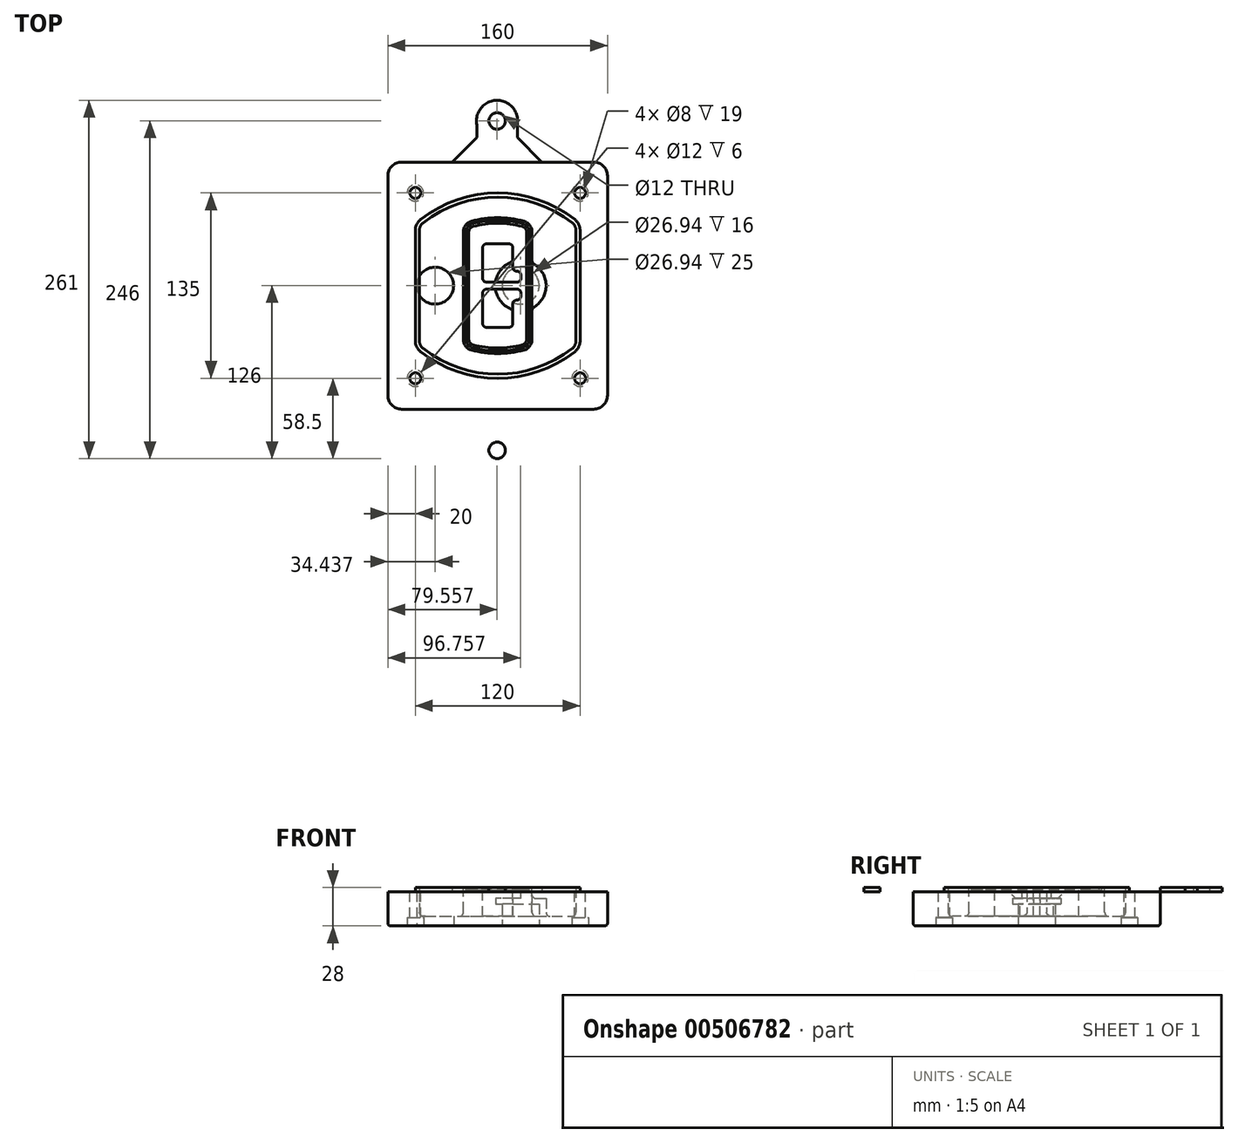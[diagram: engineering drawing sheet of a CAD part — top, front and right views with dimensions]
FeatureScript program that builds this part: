
annotation { "Feature Type Name" : "Feature", "Feature Type Description" : "" }
export const myFeature = defineFeature(function(context is Context, id is Id, definition is map)
    precondition{}
    {
        {
            var Q0;
            Q0=qCreatedBy(makeId("Top.planeOp"),FACE);
            var sketch = newSketch(context, id + "F0", { "sketchPlane" : qUnion([Q0])});
            skPoint(sketch, "E0.rect.middle", {"position": v(0, 0) * mm});
            skLineSegment(sketch, "E1.bottom", {"start": v(-70, -90) * mm, "end": v(70, -90) * mm});
            skLineSegment(sketch, "E1.top", {"start": v(-70, 90) * mm, "end": v(70, 90) * mm});
            skLineSegment(sketch, "E1.left", {"start": v(-80, -80) * mm, "end": v(-80, 80) * mm});
            skLineSegment(sketch, "E1.right", {"start": v(80, -80) * mm, "end": v(80, 80) * mm});
            skLineSegment(sketch, "E2", {"start": v(-80, 90) * mm, "end": v(80, -90) * mm, "construction": true});
            skLineSegment(sketch, "E3", {"start": v(80, 90) * mm, "end": v(-80, -90) * mm, "construction": true});
            skCircle(sketch, "E4", {"center": v(-60, 67.5) * mm, "radius": 4 * mm});
            skCircle(sketch, "E5", {"center": v(60, 67.5) * mm, "radius": 4 * mm});
            skCircle(sketch, "E6", {"center": v(60, -67.5) * mm, "radius": 4 * mm});
            skCircle(sketch, "E7", {"center": v(-60, -67.5) * mm, "radius": 4 * mm});
            skLineSegment(sketch, "E8", {"start": v(-60, 67.5) * mm, "end": v(60, 67.5) * mm, "construction": true});
            skLineSegment(sketch, "E9", {"start": v(60, 67.5) * mm, "end": v(60, -67.5) * mm, "construction": true});
            skLineSegment(sketch, "E10", {"start": v(60, -67.5) * mm, "end": v(-60, -67.5) * mm, "construction": true});
            skLineSegment(sketch, "E11", {"start": v(-60, -67.5) * mm, "end": v(-60, 67.5) * mm, "construction": true});
            skLineSegment(sketch, "E12", {"start": v(-60, 40.3) * mm, "end": v(-60, -40.3) * mm});
            skLineSegment(sketch, "E13", {"start": v(60, 40.3) * mm, "end": v(60, -40.3) * mm});
            skArc(sketch, "E14", {"start": v(56.15, 48.18) * mm, "mid": v(0, 67.5) * mm, "end": v(-56.15, 48.18) * mm});
            skArc(sketch, "E15", {"start": v(-56.15, -48.18) * mm, "mid": v(0, -67.5) * mm, "end": v(56.15, -48.18) * mm});
            skLineSegment(sketch, "E16", {"start": v(-60, 0) * mm, "end": v(60, 0) * mm, "construction": true});
            skPoint(sketch, "E17.visualSharp", {"position": v(-60, -45) * mm});
            skArc(sketch, "E17.filletArc", {"start": v(-60, -40.3) * mm, "mid": v(-58.99, -44.68) * mm, "end": v(-56.15, -48.18) * mm});
            skPoint(sketch, "E18.visualSharp", {"position": v(-60, 45) * mm});
            skArc(sketch, "E18.filletArc", {"start": v(-56.15, 48.18) * mm, "mid": v(-58.99, 44.68) * mm, "end": v(-60, 40.3) * mm});
            skPoint(sketch, "E19.visualSharp", {"position": v(60, 45) * mm});
            skArc(sketch, "E19.filletArc", {"start": v(60, 40.3) * mm, "mid": v(58.99, 44.68) * mm, "end": v(56.15, 48.18) * mm});
            skPoint(sketch, "E20.visualSharp", {"position": v(60, -45) * mm});
            skArc(sketch, "E20.filletArc", {"start": v(56.15, -48.18) * mm, "mid": v(58.99, -44.68) * mm, "end": v(60, -40.3) * mm});
            skPoint(sketch, "E21.visualSharp", {"position": v(-80, 90) * mm});
            skArc(sketch, "E21.filletArc", {"start": v(-70, 90) * mm, "mid": v(-77.07, 87.07) * mm, "end": v(-80, 80) * mm});
            skPoint(sketch, "E22.visualSharp", {"position": v(80, 90) * mm});
            skArc(sketch, "E22.filletArc", {"start": v(80, 80) * mm, "mid": v(77.07, 87.07) * mm, "end": v(70, 90) * mm});
            skPoint(sketch, "E23.visualSharp", {"position": v(80, -90) * mm});
            skArc(sketch, "E23.filletArc", {"start": v(70, -90) * mm, "mid": v(77.07, -87.07) * mm, "end": v(80, -80) * mm});
            skPoint(sketch, "E24.visualSharp", {"position": v(-80, -90) * mm});
            skArc(sketch, "E24.filletArc", {"start": v(-80, -80) * mm, "mid": v(-77.07, -87.07) * mm, "end": v(-70, -90) * mm});
            skArc(sketch, "E25.0", {"start": v(57, 40.3) * mm, "mid": v(56.3, 43.36) * mm, "end": v(54.3, 45.81) * mm});
            skLineSegment(sketch, "E25.1", {"start": v(57, 40.3) * mm, "end": v(57, -40.3) * mm});
            skArc(sketch, "E25.2", {"start": v(54.3, -45.81) * mm, "mid": v(56.3, -43.36) * mm, "end": v(57, -40.3) * mm});
            skArc(sketch, "E25.3", {"start": v(-54.3, -45.81) * mm, "mid": v(0, -64.5) * mm, "end": v(54.3, -45.81) * mm});
            skArc(sketch, "E25.4", {"start": v(-57, -40.3) * mm, "mid": v(-56.3, -43.36) * mm, "end": v(-54.3, -45.81) * mm});
            skArc(sketch, "E25.5", {"start": v(54.3, 45.81) * mm, "mid": v(0, 64.5) * mm, "end": v(-54.3, 45.81) * mm});
            skLineSegment(sketch, "E25.6", {"start": v(-57, 40.3) * mm, "end": v(-57, -40.3) * mm});
            skArc(sketch, "E25.7", {"start": v(-54.3, 45.81) * mm, "mid": v(-56.3, 43.36) * mm, "end": v(-57, 40.3) * mm});
            skArc(sketch, "E26.0", {"start": v(-58.62, 51.33) * mm, "mid": v(-62.58, 46.43) * mm, "end": v(-64, 40.3) * mm});
            skArc(sketch, "E26.1", {"start": v(58.62, 51.33) * mm, "mid": v(0, 71.5) * mm, "end": v(-58.62, 51.33) * mm});
            skArc(sketch, "E26.2", {"start": v(64, 40.3) * mm, "mid": v(62.58, 46.43) * mm, "end": v(58.62, 51.33) * mm});
            skLineSegment(sketch, "E26.3", {"start": v(64, 40.3) * mm, "end": v(64, -40.3) * mm});
            skArc(sketch, "E26.4", {"start": v(58.62, -51.33) * mm, "mid": v(62.58, -46.43) * mm, "end": v(64, -40.3) * mm});
            skLineSegment(sketch, "E26.5", {"start": v(-64, 40.3) * mm, "end": v(-64, -40.3) * mm});
            skArc(sketch, "E26.6", {"start": v(-58.62, -51.33) * mm, "mid": v(0, -71.5) * mm, "end": v(58.62, -51.33) * mm});
            skArc(sketch, "E26.7", {"start": v(-64, -40.3) * mm, "mid": v(-62.58, -46.43) * mm, "end": v(-58.62, -51.33) * mm});
            skSolve(sketch);
        }
        {
            var Q0;
            Q0=makeQuery(id+"F0.imprint","IMPRINT",FACE,{"disambiguationData":[TD([[makeQuery(id+"F0.imprint","IMPRINT",EDGE,{"derivedFrom":sQuery(id+"F0.wireOp",EDGE,"E1.bottom")}),1.0]])]});
            var Q1;
            Q1=makeQuery(id+"F0.imprint","IMPRINT",FACE,{"disambiguationData":[TD([[makeQuery(id+"F0.imprint","IMPRINT",EDGE,{"derivedFrom":sQuery(id+"F0.wireOp",EDGE,"E12")}),1.0]])]});
            var Q2;
            Q2=makeQuery(id+"F0.imprint","IMPRINT",FACE,{"disambiguationData":[TD([[makeQuery(id+"F0.imprint","IMPRINT",EDGE,{"derivedFrom":sQuery(id+"F0.wireOp",EDGE,"E25.0")}),1.0]])]});
            var Q3;
            Q3=makeQuery(id+"F0.imprint","IMPRINT",FACE,{"disambiguationData":[TD([[makeQuery(id+"F0.imprint","IMPRINT",EDGE,{"derivedFrom":sQuery(id+"F0.wireOp",EDGE,"E12")}),-1.0]])]});
            extrude(context, id + "F1", {"entities" : qUnion([Q0, Q1, Q2, Q3]), "oppositeDirection" : true, "depth" : 25 * mm});
        }
        {
            var Q0;
            Q0=makeQuery(id+"F0.imprint","IMPRINT",FACE,{"disambiguationData":[TD([[makeQuery(id+"F0.imprint","IMPRINT",EDGE,{"derivedFrom":sQuery(id+"F0.wireOp",EDGE,"E12")}),1.0]])]});
            extrude(context, id + "F2", {"entities" : qUnion([Q0]), "operationType" : NewBodyOperationType.ADD, "depth" : 3 * mm});
        }
        {
            var Q0;
            Q0=makeQuery(id+"F0.imprint","IMPRINT",FACE,{"disambiguationData":[TD([[makeQuery(id+"F0.imprint","IMPRINT",EDGE,{"derivedFrom":sQuery(id+"F0.wireOp",EDGE,"E25.0")}),1.0]])]});
            extrude(context, id + "F3", {"entities" : qUnion([Q0]), "operationType" : NewBodyOperationType.REMOVE, "oppositeDirection" : true, "depth" : 18 * mm});
        }
        {
            var Q0;
            Q0=makeQuery(id+"F2.opExtrude","CAP_FACE",FACE,{"disambiguationData":[OSD([sQuery(id+"F0.wireOp",EDGE,"E12"),sQuery(id+"F0.wireOp",EDGE,"E13"),sQuery(id+"F0.wireOp",EDGE,"E14"),sQuery(id+"F0.wireOp",EDGE,"E15"),sQuery(id+"F0.wireOp",EDGE,"E17.filletArc"),sQuery(id+"F0.wireOp",EDGE,"E18.filletArc"),sQuery(id+"F0.wireOp",EDGE,"E19.filletArc"),sQuery(id+"F0.wireOp",EDGE,"E20.filletArc"),sQuery(id+"F0.wireOp",EDGE,"E25.0"),sQuery(id+"F0.wireOp",EDGE,"E25.1"),sQuery(id+"F0.wireOp",EDGE,"E25.2"),sQuery(id+"F0.wireOp",EDGE,"E25.3"),sQuery(id+"F0.wireOp",EDGE,"E25.4"),sQuery(id+"F0.wireOp",EDGE,"E25.5"),sQuery(id+"F0.wireOp",EDGE,"E25.6"),sQuery(id+"F0.wireOp",EDGE,"E25.7")])],"isStart":false});
            var sketch = newSketch(context, id + "F4", { "sketchPlane" : qUnion([Q0])});
            skArc(sketch, "E27.0", {"start": v(-19.08, -46.97) * mm, "mid": v(0, -49.5) * mm, "end": v(19.08, -46.97) * mm});
            skArc(sketch, "E28.0", {"start": v(19.08, 46.97) * mm, "mid": v(0, 49.5) * mm, "end": v(-19.08, 46.97) * mm});
            skLineSegment(sketch, "E29", {"start": v(-25, 39.25) * mm, "end": v(-25, -39.25) * mm});
            skLineSegment(sketch, "E30", {"start": v(25, 39.25) * mm, "end": v(25, -39.25) * mm});
            skLineSegment(sketch, "E31", {"start": v(-25, 45.1) * mm, "end": v(25, 45.1) * mm, "construction": true});
            skLineSegment(sketch, "E32", {"start": v(-25, -45.1) * mm, "end": v(25, -45.1) * mm, "construction": true});
            skPoint(sketch, "E33.visualSharp", {"position": v(-25, 45.1) * mm});
            skArc(sketch, "E33.filletArc", {"start": v(-19.08, 46.97) * mm, "mid": v(-23.35, 44.11) * mm, "end": v(-25, 39.25) * mm});
            skPoint(sketch, "E34.visualSharp", {"position": v(25, 45.1) * mm});
            skArc(sketch, "E34.filletArc", {"start": v(25, 39.25) * mm, "mid": v(23.35, 44.11) * mm, "end": v(19.08, 46.97) * mm});
            skPoint(sketch, "E35.visualSharp", {"position": v(25, -45.1) * mm});
            skArc(sketch, "E35.filletArc", {"start": v(19.08, -46.97) * mm, "mid": v(23.35, -44.11) * mm, "end": v(25, -39.25) * mm});
            skPoint(sketch, "E36.visualSharp", {"position": v(-25, -45.1) * mm});
            skArc(sketch, "E36.filletArc", {"start": v(-25, -39.25) * mm, "mid": v(-23.35, -44.11) * mm, "end": v(-19.08, -46.97) * mm});
            skArc(sketch, "E37.0", {"start": v(54.3, 45.81) * mm, "mid": v(0, 64.5) * mm, "end": v(-54.3, 45.81) * mm});
            skArc(sketch, "E37.1", {"start": v(-54.3, 45.81) * mm, "mid": v(-56.3, 43.36) * mm, "end": v(-57, 40.3) * mm});
            skLineSegment(sketch, "E37.2", {"start": v(-57, 40.3) * mm, "end": v(-57, -40.3) * mm});
            skArc(sketch, "E37.3", {"start": v(-57, -40.3) * mm, "mid": v(-56.3, -43.36) * mm, "end": v(-54.3, -45.81) * mm});
            skArc(sketch, "E37.4", {"start": v(-54.3, -45.81) * mm, "mid": v(0, -64.5) * mm, "end": v(54.3, -45.81) * mm});
            skArc(sketch, "E37.5", {"start": v(54.3, -45.81) * mm, "mid": v(56.3, -43.36) * mm, "end": v(57, -40.3) * mm});
            skLineSegment(sketch, "E37.6", {"start": v(57, 40.3) * mm, "end": v(57, -40.3) * mm});
            skArc(sketch, "E37.7", {"start": v(57, 40.3) * mm, "mid": v(56.3, 43.36) * mm, "end": v(54.3, 45.81) * mm});
            skLineSegment(sketch, "E38.0", {"start": v(23, 39.25) * mm, "end": v(23, -39.25) * mm});
            skArc(sketch, "E38.1", {"start": v(18.56, -45.04) * mm, "mid": v(21.76, -42.9) * mm, "end": v(23, -39.25) * mm});
            skArc(sketch, "E38.2", {"start": v(-18.56, -45.04) * mm, "mid": v(0, -47.5) * mm, "end": v(18.56, -45.04) * mm});
            skArc(sketch, "E38.3", {"start": v(-23, -39.25) * mm, "mid": v(-21.76, -42.9) * mm, "end": v(-18.56, -45.04) * mm});
            skLineSegment(sketch, "E38.4", {"start": v(-23, 39.25) * mm, "end": v(-23, -39.25) * mm});
            skArc(sketch, "E38.5", {"start": v(23, 39.25) * mm, "mid": v(21.76, 42.9) * mm, "end": v(18.56, 45.04) * mm});
            skArc(sketch, "E38.6", {"start": v(-18.56, 45.04) * mm, "mid": v(-21.76, 42.9) * mm, "end": v(-23, 39.25) * mm});
            skArc(sketch, "E38.7", {"start": v(18.56, 45.04) * mm, "mid": v(0, 47.5) * mm, "end": v(-18.56, 45.04) * mm});
            skArc(sketch, "E39.0", {"start": v(21, 39.25) * mm, "mid": v(20.18, 41.68) * mm, "end": v(18.04, 43.1) * mm});
            skLineSegment(sketch, "E39.1", {"start": v(21, 39.25) * mm, "end": v(21, -39.25) * mm});
            skArc(sketch, "E39.2", {"start": v(18.04, -43.1) * mm, "mid": v(20.18, -41.68) * mm, "end": v(21, -39.25) * mm});
            skArc(sketch, "E39.3", {"start": v(-18.04, -43.1) * mm, "mid": v(0, -45.5) * mm, "end": v(18.04, -43.1) * mm});
            skArc(sketch, "E39.4", {"start": v(-21, -39.25) * mm, "mid": v(-20.18, -41.68) * mm, "end": v(-18.04, -43.1) * mm});
            skArc(sketch, "E39.5", {"start": v(18.04, 43.1) * mm, "mid": v(0, 45.5) * mm, "end": v(-18.04, 43.1) * mm});
            skLineSegment(sketch, "E39.6", {"start": v(-21, 39.25) * mm, "end": v(-21, -39.25) * mm});
            skArc(sketch, "E39.7", {"start": v(-18.04, 43.1) * mm, "mid": v(-20.18, 41.68) * mm, "end": v(-21, 39.25) * mm});
            skLineSegment(sketch, "E40", {"start": v(-25, 0) * mm, "end": v(25, 0) * mm, "construction": true});
            skLineSegment(sketch, "E41", {"start": v(-11, 5.5) * mm, "end": v(-11, 27.5) * mm});
            skLineSegment(sketch, "E42", {"start": v(-8, 30.5) * mm, "end": v(8, 30.5) * mm});
            skLineSegment(sketch, "E43", {"start": v(11, 27.5) * mm, "end": v(11, 13.5) * mm});
            skLineSegment(sketch, "E44", {"start": v(14, 10.5) * mm, "end": v(14, 10.5) * mm});
            skLineSegment(sketch, "E45", {"start": v(17, 7.5) * mm, "end": v(17, 5.5) * mm});
            skLineSegment(sketch, "E46", {"start": v(14, 2.5) * mm, "end": v(-8, 2.5) * mm});
            skPoint(sketch, "E47.visualSharp", {"position": v(-11, 30.5) * mm});
            skArc(sketch, "E47.filletArc", {"start": v(-8, 30.5) * mm, "mid": v(-10.12, 29.62) * mm, "end": v(-11, 27.5) * mm});
            skPoint(sketch, "E48.visualSharp", {"position": v(11, 30.5) * mm});
            skArc(sketch, "E48.filletArc", {"start": v(11, 27.5) * mm, "mid": v(10.12, 29.62) * mm, "end": v(8, 30.5) * mm});
            skPoint(sketch, "E49.visualSharp", {"position": v(11, 10.5) * mm});
            skArc(sketch, "E49.filletArc", {"start": v(11, 13.5) * mm, "mid": v(11.88, 11.38) * mm, "end": v(14, 10.5) * mm});
            skPoint(sketch, "E50.visualSharp", {"position": v(17, 10.5) * mm});
            skArc(sketch, "E50.filletArc", {"start": v(17, 7.5) * mm, "mid": v(16.12, 9.62) * mm, "end": v(14, 10.5) * mm});
            skPoint(sketch, "E51.visualSharp", {"position": v(17, 2.5) * mm});
            skArc(sketch, "E51.filletArc", {"start": v(14, 2.5) * mm, "mid": v(16.12, 3.38) * mm, "end": v(17, 5.5) * mm});
            skPoint(sketch, "E52.visualSharp", {"position": v(-11, 2.5) * mm});
            skArc(sketch, "E52.filletArc", {"start": v(-11, 5.5) * mm, "mid": v(-10.12, 3.38) * mm, "end": v(-8, 2.5) * mm});
            skLineSegment(sketch, "E53.0.MirrorCS", {"start": v(14, -2.5) * mm, "end": v(-8, -2.5) * mm});
            skArc(sketch, "E54.0.MirrorCS", {"start": v(-11, -5.5) * mm, "mid": v(-10.12, -3.38) * mm, "end": v(-8, -2.5) * mm});
            skLineSegment(sketch, "E55.0.MirrorCS", {"start": v(-11, -5.5) * mm, "end": v(-11, -27.5) * mm});
            skArc(sketch, "E56.0.MirrorCS", {"start": v(-8, -30.5) * mm, "mid": v(-10.12, -29.62) * mm, "end": v(-11, -27.5) * mm});
            skLineSegment(sketch, "E57.0.MirrorCS", {"start": v(-8, -30.5) * mm, "end": v(8, -30.5) * mm});
            skArc(sketch, "E58.0.MirrorCS", {"start": v(11, -27.5) * mm, "mid": v(10.12, -29.62) * mm, "end": v(8, -30.5) * mm});
            skLineSegment(sketch, "E59.0.MirrorCS", {"start": v(11, -27.5) * mm, "end": v(11, -13.5) * mm});
            skArc(sketch, "E60.0.MirrorCS", {"start": v(11, -13.5) * mm, "mid": v(11.88, -11.38) * mm, "end": v(14, -10.5) * mm});
            skArc(sketch, "E61.0.MirrorCS", {"start": v(17, -7.5) * mm, "mid": v(16.12, -9.62) * mm, "end": v(14, -10.5) * mm});
            skLineSegment(sketch, "E62.0.MirrorCS", {"start": v(17, -7.5) * mm, "end": v(17, -5.5) * mm});
            skArc(sketch, "E63.0.MirrorCS", {"start": v(14, -2.5) * mm, "mid": v(16.12, -3.38) * mm, "end": v(17, -5.5) * mm});
            skSolve(sketch);
        }
        {
            var Q0;
            Q0=makeQuery(id+"F4.imprint","IMPRINT",FACE,{"disambiguationData":[TD([[makeQuery(id+"F4.imprint","IMPRINT",EDGE,{"derivedFrom":sQuery(id+"F4.wireOp",EDGE,"E27.0")}),1.0]])]});
            var Q1;
            Q1=makeQuery(id+"F4.imprint","IMPRINT",FACE,{"disambiguationData":[TD([[makeQuery(id+"F4.imprint","IMPRINT",EDGE,{"derivedFrom":sQuery(id+"F4.wireOp",EDGE,"E38.0")}),-1.0]])]});
            var Q2;
            Q2=makeQuery(id+"F4.imprint","IMPRINT",FACE,{"disambiguationData":[TD([[makeQuery(id+"F4.imprint","IMPRINT",EDGE,{"derivedFrom":sQuery(id+"F4.wireOp",EDGE,"E39.0")}),1.0]])]});
            extrude(context, id + "F5", {"entities" : qUnion([Q0, Q1, Q2]), "operationType" : NewBodyOperationType.ADD, "endBound" : BoundingType.UP_TO_NEXT, "oppositeDirection" : true, "depth" : 25 * mm});
        }
        {
            var Q0;
            Q0=makeQuery(id+"F4.imprint","IMPRINT",FACE,{"disambiguationData":[TD([[makeQuery(id+"F4.imprint","IMPRINT",EDGE,{"derivedFrom":sQuery(id+"F4.wireOp",EDGE,"E38.0")}),-1.0]])]});
            extrude(context, id + "F6", {"entities" : qUnion([Q0]), "operationType" : NewBodyOperationType.REMOVE, "oppositeDirection" : true, "depth" : 2 * mm});
        }
        {
            var Q0;
            Q0=makeQuery(id+"F1.opExtrude","CAP_FACE",FACE,{"disambiguationData":[OSD([sQuery(id+"F0.wireOp",EDGE,"E1.bottom"),sQuery(id+"F0.wireOp",EDGE,"E1.top"),sQuery(id+"F0.wireOp",EDGE,"E1.left"),sQuery(id+"F0.wireOp",EDGE,"E1.right"),sQuery(id+"F0.wireOp",EDGE,"E4"),sQuery(id+"F0.wireOp",EDGE,"E5"),sQuery(id+"F0.wireOp",EDGE,"E6"),sQuery(id+"F0.wireOp",EDGE,"E7"),sQuery(id+"F0.wireOp",EDGE,"E21.filletArc"),sQuery(id+"F0.wireOp",EDGE,"E22.filletArc"),sQuery(id+"F0.wireOp",EDGE,"E23.filletArc"),sQuery(id+"F0.wireOp",EDGE,"E24.filletArc")])],"isStart":false});
            var sketch = newSketch(context, id + "F7", { "sketchPlane" : qUnion([Q0])});
            skCircle(sketch, "E64", {"center": v(16.76, 0) * mm, "radius": 13.47 * mm});
            skCircle(sketch, "E65", {"center": v(-45.56, 0) * mm, "radius": 13.47 * mm});
            skLineSegment(sketch, "E66", {"start": v(80, 0) * mm, "end": v(-80, 0) * mm});
            skCircle(sketch, "E67", {"center": v(16.76, 0) * mm, "radius": 18.47 * mm});
            skCircle(sketch, "E68", {"center": v(60, -67.5) * mm, "radius": 6 * mm});
            skCircle(sketch, "E69", {"center": v(-60, -67.5) * mm, "radius": 6 * mm});
            skCircle(sketch, "E70", {"center": v(-60, 67.5) * mm, "radius": 6 * mm});
            skCircle(sketch, "E71", {"center": v(60, 67.5) * mm, "radius": 6 * mm});
            skSolve(sketch);
        }
        {
            var Q0;
            {var subQ1=sQuery(id+"F7.wireOp",EDGE,"E66");var subQ4=sQuery(id+"F7.wireOp",EDGE,"E64");var subQ6=makeQuery(id+"F7.imprint","INTERSECT",VERTEX,{"disambiguationData":[OD(0.0)],"derivedFrom":[subQ4,subQ1]});Q0=makeQuery(id+"F7.imprint","IMPRINT",FACE,{"disambiguationData":[TD([[makeQuery(id+"F7.imprint","IMPRINT",EDGE,{"disambiguationData":[TD([[subQ6,-1.0]])],"derivedFrom":subQ4}),-1.0]])]});}
            var Q1;
            {var subQ0=sQuery(id+"F7.wireOp",EDGE,"E66");var subQ1=sQuery(id+"F7.wireOp",EDGE,"E64");var subQ3=makeQuery(id+"F7.imprint","INTERSECT",VERTEX,{"disambiguationData":[OD(0.0)],"derivedFrom":[subQ1,subQ0]});Q1=makeQuery(id+"F7.imprint","IMPRINT",FACE,{"disambiguationData":[TD([[makeQuery(id+"F7.imprint","IMPRINT",EDGE,{"disambiguationData":[TD([[subQ3,-1.0]])],"derivedFrom":subQ1}),1.0]])]});}
            var Q2;
            {var subQ0=sQuery(id+"F7.wireOp",EDGE,"E66");var subQ1=sQuery(id+"F7.wireOp",EDGE,"E64");var subQ3=makeQuery(id+"F7.imprint","INTERSECT",VERTEX,{"disambiguationData":[OD(0.0)],"derivedFrom":[subQ1,subQ0]});Q2=makeQuery(id+"F7.imprint","IMPRINT",FACE,{"disambiguationData":[TD([[makeQuery(id+"F7.imprint","IMPRINT",EDGE,{"disambiguationData":[TD([[subQ3,1.0]])],"derivedFrom":subQ1}),1.0]])]});}
            var Q3;
            {var subQ1=sQuery(id+"F7.wireOp",EDGE,"E66");var subQ4=sQuery(id+"F7.wireOp",EDGE,"E64");var subQ6=makeQuery(id+"F7.imprint","INTERSECT",VERTEX,{"disambiguationData":[OD(0.0)],"derivedFrom":[subQ4,subQ1]});Q3=makeQuery(id+"F7.imprint","IMPRINT",FACE,{"disambiguationData":[TD([[makeQuery(id+"F7.imprint","IMPRINT",EDGE,{"disambiguationData":[TD([[subQ6,1.0]])],"derivedFrom":subQ4}),-1.0]])]});}
            extrude(context, id + "F8", {"entities" : qUnion([Q0, Q1, Q2, Q3]), "operationType" : NewBodyOperationType.ADD, "oppositeDirection" : true, "depth" : 20 * mm});
        }
        {
            var Q0;
            {var subQ0=sQuery(id+"F7.wireOp",EDGE,"E66");var subQ1=sQuery(id+"F7.wireOp",EDGE,"E64");var subQ3=makeQuery(id+"F7.imprint","INTERSECT",VERTEX,{"disambiguationData":[OD(0.0)],"derivedFrom":[subQ1,subQ0]});Q0=makeQuery(id+"F7.imprint","IMPRINT",FACE,{"disambiguationData":[TD([[makeQuery(id+"F7.imprint","IMPRINT",EDGE,{"disambiguationData":[TD([[subQ3,-1.0]])],"derivedFrom":subQ1}),1.0]])]});}
            var Q1;
            {var subQ0=sQuery(id+"F7.wireOp",EDGE,"E66");var subQ1=sQuery(id+"F7.wireOp",EDGE,"E64");var subQ3=makeQuery(id+"F7.imprint","INTERSECT",VERTEX,{"disambiguationData":[OD(0.0)],"derivedFrom":[subQ1,subQ0]});Q1=makeQuery(id+"F7.imprint","IMPRINT",FACE,{"disambiguationData":[TD([[makeQuery(id+"F7.imprint","IMPRINT",EDGE,{"disambiguationData":[TD([[subQ3,1.0]])],"derivedFrom":subQ1}),1.0]])]});}
            extrude(context, id + "F9", {"entities" : qUnion([Q0, Q1]), "operationType" : NewBodyOperationType.REMOVE, "oppositeDirection" : true, "depth" : 16 * mm});
        }
        {
            var Q0;
            {var subQ0=sQuery(id+"F7.wireOp",EDGE,"E66");var subQ1=sQuery(id+"F7.wireOp",EDGE,"E65");var subQ3=makeQuery(id+"F7.imprint","INTERSECT",VERTEX,{"disambiguationData":[OD(0.0)],"derivedFrom":[subQ1,subQ0]});Q0=makeQuery(id+"F7.imprint","IMPRINT",FACE,{"disambiguationData":[TD([[makeQuery(id+"F7.imprint","IMPRINT",EDGE,{"disambiguationData":[TD([[subQ3,-1.0]])],"derivedFrom":subQ1}),1.0]])]});}
            var Q1;
            {var subQ0=sQuery(id+"F7.wireOp",EDGE,"E66");var subQ1=sQuery(id+"F7.wireOp",EDGE,"E65");var subQ3=makeQuery(id+"F7.imprint","INTERSECT",VERTEX,{"disambiguationData":[OD(0.0)],"derivedFrom":[subQ1,subQ0]});Q1=makeQuery(id+"F7.imprint","IMPRINT",FACE,{"disambiguationData":[TD([[makeQuery(id+"F7.imprint","IMPRINT",EDGE,{"disambiguationData":[TD([[subQ3,1.0]])],"derivedFrom":subQ1}),1.0]])]});}
            extrude(context, id + "F10", {"entities" : qUnion([Q0, Q1]), "operationType" : NewBodyOperationType.REMOVE, "oppositeDirection" : true, "depth" : 25 * mm});
        }
        {
            var Q0;
            Q0=makeQuery(id+"F7.imprint","IMPRINT",FACE,{"disambiguationData":[TD([[makeQuery(id+"F7.imprint","IMPRINT",EDGE,{"derivedFrom":sQuery(id+"F7.wireOp",EDGE,"E68")}),1.0]])]});
            var Q1;
            Q1=makeQuery(id+"F7.imprint","IMPRINT",FACE,{"disambiguationData":[TD([[makeQuery(id+"F7.imprint","IMPRINT",EDGE,{"derivedFrom":makeQuery(id+"F1.opExtrude","CAP_EDGE",EDGE,{"disambiguationData":[OSD([sQuery(id+"F0.wireOp",EDGE,"E5")])],"isStart":false})}),-1.0]])]});
            var Q2;
            Q2=makeQuery(id+"F7.imprint","IMPRINT",FACE,{"disambiguationData":[TD([[makeQuery(id+"F7.imprint","IMPRINT",EDGE,{"derivedFrom":sQuery(id+"F7.wireOp",EDGE,"E69")}),1.0]])]});
            var Q3;
            Q3=makeQuery(id+"F7.imprint","IMPRINT",FACE,{"disambiguationData":[TD([[makeQuery(id+"F7.imprint","IMPRINT",EDGE,{"derivedFrom":makeQuery(id+"F1.opExtrude","CAP_EDGE",EDGE,{"disambiguationData":[OSD([sQuery(id+"F0.wireOp",EDGE,"E4")])],"isStart":false})}),-1.0]])]});
            var Q4;
            Q4=makeQuery(id+"F7.imprint","IMPRINT",FACE,{"disambiguationData":[TD([[makeQuery(id+"F7.imprint","IMPRINT",EDGE,{"derivedFrom":sQuery(id+"F7.wireOp",EDGE,"E70")}),1.0]])]});
            var Q5;
            Q5=makeQuery(id+"F7.imprint","IMPRINT",FACE,{"disambiguationData":[TD([[makeQuery(id+"F7.imprint","IMPRINT",EDGE,{"derivedFrom":makeQuery(id+"F1.opExtrude","CAP_EDGE",EDGE,{"disambiguationData":[OSD([sQuery(id+"F0.wireOp",EDGE,"E7")])],"isStart":false})}),-1.0]])]});
            var Q6;
            Q6=makeQuery(id+"F7.imprint","IMPRINT",FACE,{"disambiguationData":[TD([[makeQuery(id+"F7.imprint","IMPRINT",EDGE,{"derivedFrom":sQuery(id+"F7.wireOp",EDGE,"E71")}),1.0]])]});
            var Q7;
            Q7=makeQuery(id+"F7.imprint","IMPRINT",FACE,{"disambiguationData":[TD([[makeQuery(id+"F7.imprint","IMPRINT",EDGE,{"derivedFrom":makeQuery(id+"F1.opExtrude","CAP_EDGE",EDGE,{"disambiguationData":[OSD([sQuery(id+"F0.wireOp",EDGE,"E6")])],"isStart":false})}),-1.0]])]});
            extrude(context, id + "F11", {"entities" : qUnion([Q0, Q1, Q2, Q3, Q4, Q5, Q6, Q7]), "operationType" : NewBodyOperationType.REMOVE, "oppositeDirection" : true, "depth" : 6 * mm});
        }
        {
            var Q0;
            Q0=makeQuery(id+"F9.boolean.opBoolean","COPY",FACE,{"derivedFrom":makeQuery(id+"F9.opExtrude","CAP_FACE",FACE,{"disambiguationData":[OSD([sQuery(id+"F7.wireOp",EDGE,"E64")])],"isStart":false})});
            var sketch = newSketch(context, id + "F12", { "sketchPlane" : qUnion([Q0])});
            skArc(sketch, "E72.0", {"start": v(11, 17.55) * mm, "mid": v(2.57, 11.82) * mm, "end": v(-1.54, 2.5) * mm});
            skArc(sketch, "E72.1", {"start": v(-1.54, -2.5) * mm, "mid": v(2.57, -11.82) * mm, "end": v(11, -17.55) * mm});
            skLineSegment(sketch, "E73", {"start": v(-1.54, -2.5) * mm, "end": v(14, -2.5) * mm});
            skLineSegment(sketch, "E74.0", {"start": v(14, 2.5) * mm, "end": v(-1.54, 2.5) * mm});
            skArc(sketch, "E74.1", {"start": v(14, 2.5) * mm, "mid": v(16.12, 3.38) * mm, "end": v(17, 5.5) * mm});
            skLineSegment(sketch, "E74.2", {"start": v(17, 7.5) * mm, "end": v(17, 5.5) * mm});
            skArc(sketch, "E74.3", {"start": v(17, 7.5) * mm, "mid": v(16.12, 9.62) * mm, "end": v(14, 10.5) * mm});
            skArc(sketch, "E74.4", {"start": v(11, 13.5) * mm, "mid": v(11.88, 11.38) * mm, "end": v(14, 10.5) * mm});
            skLineSegment(sketch, "E74.5", {"start": v(11, 17.55) * mm, "end": v(11, 13.5) * mm});
            skLineSegment(sketch, "E74.7", {"start": v(14, -2.5) * mm, "end": v(-1.54, -2.5) * mm});
            skArc(sketch, "E74.8", {"start": v(14, -2.5) * mm, "mid": v(16.12, -3.38) * mm, "end": v(17, -5.5) * mm});
            skLineSegment(sketch, "E74.9", {"start": v(17, -7.5) * mm, "end": v(17, -5.5) * mm});
            skArc(sketch, "E74.10", {"start": v(17, -7.5) * mm, "mid": v(16.12, -9.62) * mm, "end": v(14, -10.5) * mm});
            skArc(sketch, "E74.11", {"start": v(11, -13.5) * mm, "mid": v(11.88, -11.38) * mm, "end": v(14, -10.5) * mm});
            skLineSegment(sketch, "E74.12", {"start": v(11, -17.55) * mm, "end": v(11, -13.5) * mm});
            skPoint(sketch, "E75.orphan", {"position": v(11, -27.5) * mm});
            skPoint(sketch, "E76.orphan", {"position": v(-8, -2.5) * mm});
            skPoint(sketch, "E77.orphan", {"position": v(-8, 2.5) * mm});
            skPoint(sketch, "E78.orphan", {"position": v(11, 27.5) * mm});
            skSolve(sketch);
        }
        {
            var Q0;
            {var subQ7=sQuery(id+"F12.wireOp",EDGE,"E72.0");var subQ14=sQuery(id+"F12.wireOp",EDGE,"E72.1");var subQ16=sQuery(id+"F12.wireOp",EDGE,"E74.1");var subQ18=sQuery(id+"F12.wireOp",EDGE,"E74.8");Q0=qUnion([makeQuery(id+"F12.imprint","IMPRINT",FACE,{"disambiguationData":[TD([[makeQuery(id+"F12.imprint","IMPRINT",EDGE,{"derivedFrom":subQ7}),1.0]])]}),makeQuery(id+"F12.imprint","IMPRINT",FACE,{"disambiguationData":[TD([[makeQuery(id+"F12.imprint","IMPRINT",EDGE,{"derivedFrom":subQ14}),1.0]])]}),makeQuery(id+"F12.imprint","IMPRINT",FACE,{"disambiguationData":[TD([[makeQuery(id+"F12.imprint","IMPRINT",EDGE,{"derivedFrom":subQ16}),1.0]])]}),makeQuery(id+"F12.imprint","IMPRINT",FACE,{"disambiguationData":[TD([[makeQuery(id+"F12.imprint","IMPRINT",EDGE,{"derivedFrom":subQ18}),-1.0]])]})]);}
            var Q1;
            Q1=makeQuery(id+"F5.boolean.opBoolean","SPLIT",FACE,{"disambiguationData":[TD([makeQuery(id+"F5.opExtrude","SWEPT_FACE",FACE,{"disambiguationData":[OSD([sQuery(id+"F4.wireOp",EDGE,"E41")])]})])],"derivedFrom":makeQuery(id+"F3.boolean.opBoolean","COPY",FACE,{"derivedFrom":makeQuery(id+"F3.opExtrude","CAP_FACE",FACE,{"disambiguationData":[OSD([sQuery(id+"F0.wireOp",EDGE,"E25.0"),sQuery(id+"F0.wireOp",EDGE,"E25.1"),sQuery(id+"F0.wireOp",EDGE,"E25.2"),sQuery(id+"F0.wireOp",EDGE,"E25.3"),sQuery(id+"F0.wireOp",EDGE,"E25.4"),sQuery(id+"F0.wireOp",EDGE,"E25.5"),sQuery(id+"F0.wireOp",EDGE,"E25.6"),sQuery(id+"F0.wireOp",EDGE,"E25.7")])],"isStart":false})})});
            extrude(context, id + "F13", {"entities" : qUnion([Q0]), "operationType" : NewBodyOperationType.REMOVE, "endBound" : BoundingType.UP_TO_SURFACE, "endBoundEntityFace" : qUnion([Q1]), "depth" : 25 * mm});
        }
        {
            var Q0;
            Q0=makeQuery(id+"F3.boolean.opBoolean","COPY",EDGE,{"derivedFrom":makeQuery(id+"F3.opExtrude","CAP_EDGE",EDGE,{"disambiguationData":[OSD([sQuery(id+"F0.wireOp",EDGE,"E25.6")])],"isStart":false})});
            var Q1;
            Q1=makeQuery(id+"F8.boolean.opBoolean","INTERSECT",EDGE,{"derivedFrom":[makeQuery(id+"F5.opExtrude","SWEPT_FACE",FACE,{"disambiguationData":[OSD([sQuery(id+"F4.wireOp",EDGE,"E30")])]}),makeQuery(id+"F8.opExtrude","CAP_FACE",FACE,{"disambiguationData":[OSD([sQuery(id+"F7.wireOp",EDGE,"E67")])],"isStart":false})]});
            var Q2;
            Q2=makeQuery(id+"F8.boolean.opBoolean","INTERSECT",EDGE,{"disambiguationData":[OD(1.0)],"derivedFrom":[makeQuery(id+"F5.opExtrude","SWEPT_FACE",FACE,{"disambiguationData":[OSD([sQuery(id+"F4.wireOp",EDGE,"E30")])]}),makeQuery(id+"F8.opExtrude","SWEPT_FACE",FACE,{"disambiguationData":[OSD([sQuery(id+"F7.wireOp",EDGE,"E67")])]})]});
            var Q3;
            {var subQ0=sQuery(id+"F4.wireOp",EDGE,"E30");Q3=makeQuery(id+"F8.boolean.opBoolean","SPLIT",EDGE,{"disambiguationData":[TD([makeQuery(id+"F5.opExtrude","SWEPT_FACE",FACE,{"disambiguationData":[OSD([sQuery(id+"F4.wireOp",EDGE,"E35.filletArc")])]})])],"derivedFrom":makeQuery(id+"F5.opExtrude","CAP_EDGE",EDGE,{"disambiguationData":[OSD([subQ0])],"isStart":false})});}
            var Q4;
            {var subQ0=sQuery(id+"F0.wireOp",EDGE,"E25.7");var subQ1=sQuery(id+"F0.wireOp",EDGE,"E25.1");var subQ2=sQuery(id+"F0.wireOp",EDGE,"E25.6");var subQ3=sQuery(id+"F0.wireOp",EDGE,"E25.5");var subQ4=sQuery(id+"F0.wireOp",EDGE,"E25.4");var subQ5=sQuery(id+"F0.wireOp",EDGE,"E25.0");var subQ6=sQuery(id+"F0.wireOp",EDGE,"E25.2");var subQ7=sQuery(id+"F0.wireOp",EDGE,"E25.3");Q4=makeQuery(id+"F8.boolean.opBoolean","INTERSECT",EDGE,{"derivedFrom":[makeQuery(id+"F5.boolean.opBoolean","SPLIT",FACE,{"disambiguationData":[TD([makeQuery(id+"F2.opExtrude","SWEPT_FACE",FACE,{"disambiguationData":[OSD([subQ5])]})])],"derivedFrom":makeQuery(id+"F3.boolean.opBoolean","COPY",FACE,{"derivedFrom":makeQuery(id+"F3.opExtrude","CAP_FACE",FACE,{"disambiguationData":[OSD([subQ5,subQ1,subQ6,subQ7,subQ4,subQ3,subQ2,subQ0])],"isStart":false})})}),makeQuery(id+"F8.opExtrude","SWEPT_FACE",FACE,{"disambiguationData":[OSD([sQuery(id+"F7.wireOp",EDGE,"E67")])]})]});}
            var Q5;
            Q5=makeQuery(id+"F8.boolean.opBoolean","INTERSECT",EDGE,{"disambiguationData":[OD(0.0)],"derivedFrom":[makeQuery(id+"F5.opExtrude","SWEPT_FACE",FACE,{"disambiguationData":[OSD([sQuery(id+"F4.wireOp",EDGE,"E30")])]}),makeQuery(id+"F8.opExtrude","SWEPT_FACE",FACE,{"disambiguationData":[OSD([sQuery(id+"F7.wireOp",EDGE,"E67")])]})]});
            fillet(context, id + "F14", {"entities" : qUnion([Q0, Q1, Q2, Q3, Q4, Q5]), "radius" : 3 * mm, "tangentPropagation" : true, "allowEdgeOverflow" : false});
        }
        {
            var Q0;
            Q0=makeQuery(id+"F1.opExtrude","CAP_EDGE",EDGE,{"disambiguationData":[OSD([sQuery(id+"F0.wireOp",EDGE,"E1.bottom")])],"isStart":false});
            fillet(context, id + "F15", {"entities" : qUnion([Q0]), "radius" : 2 * mm, "tangentPropagation" : true, "allowEdgeOverflow" : false});
        }
        {
            var Q0;
            {var subQ0=sQuery(id+"F0.wireOp",EDGE,"E21.filletArc");var subQ1=sQuery(id+"F0.wireOp",EDGE,"E7");var subQ2=sQuery(id+"F0.wireOp",EDGE,"E6");var subQ3=sQuery(id+"F0.wireOp",EDGE,"E5");var subQ4=sQuery(id+"F0.wireOp",EDGE,"E4");var subQ5=sQuery(id+"F0.wireOp",EDGE,"E22.filletArc");var subQ6=sQuery(id+"F0.wireOp",EDGE,"E1.bottom");var subQ7=sQuery(id+"F0.wireOp",EDGE,"E1.right");var subQ8=sQuery(id+"F0.wireOp",EDGE,"E1.top");var subQ9=sQuery(id+"F0.wireOp",EDGE,"E1.left");var subQ10=sQuery(id+"F0.wireOp",EDGE,"E23.filletArc");var subQ11=sQuery(id+"F0.wireOp",EDGE,"E24.filletArc");Q0=makeQuery(id+"F2.boolean.opBoolean","SPLIT",FACE,{"disambiguationData":[TD([makeQuery(id+"F1.opExtrude","SWEPT_FACE",FACE,{"disambiguationData":[OSD([subQ6])]})])],"derivedFrom":makeQuery(id+"F1.opExtrude","CAP_FACE",FACE,{"disambiguationData":[OSD([subQ6,subQ8,subQ9,subQ7,subQ4,subQ3,subQ2,subQ1,subQ0,subQ5,subQ10,subQ11])],"isStart":true})});}
            var sketch = newSketch(context, id + "F16", { "sketchPlane" : qUnion([Q0])});
            skPoint(sketch, "E79.endSnap0", {"position": v(0, 90) * mm});
            skArc(sketch, "E80", {"start": v(14.27, 117.07) * mm, "mid": v(-0.44, 135) * mm, "end": v(-15.15, 117.07) * mm});
            skLineSegment(sketch, "E81", {"start": v(-0.44, 120) * mm, "end": v(0, 90) * mm, "construction": true});
            skLineSegment(sketch, "E82", {"start": v(-15.15, 117.07) * mm, "end": v(-15.15, 108) * mm});
            skLineSegment(sketch, "E83", {"start": v(-15.15, 108) * mm, "end": v(-33.15, 90) * mm});
            skLineSegment(sketch, "E84", {"start": v(14.27, 117.07) * mm, "end": v(14.27, 108) * mm});
            skLineSegment(sketch, "E85", {"start": v(14.27, 108) * mm, "end": v(32.27, 90) * mm});
            skCircle(sketch, "E86", {"center": v(-0.44, 120) * mm, "radius": 6 * mm});
            skLineSegment(sketch, "E87", {"start": v(80, 0) * mm, "end": v(-80, 0) * mm, "construction": true});
            skLineSegment(sketch, "E88.MirrorCS", {"start": v(14.27, -108) * mm, "end": v(32.27, -90) * mm});
            skLineSegment(sketch, "E89.MirrorCS", {"start": v(-15.15, -108) * mm, "end": v(-33.15, -90) * mm});
            skLineSegment(sketch, "E90.MirrorCS", {"start": v(-0.44, -120) * mm, "end": v(0, -90) * mm, "construction": true});
            skLineSegment(sketch, "E91.MirrorCS", {"start": v(-15.15, -117.07) * mm, "end": v(-15.15, -108) * mm});
            skArc(sketch, "E92.MirrorCS", {"start": v(14.27, -117.07) * mm, "mid": v(-0.44, -135) * mm, "end": v(-15.15, -117.07) * mm});
            skCircle(sketch, "E93.MirrorC", {"center": v(-0.44, -120) * mm, "radius": 6 * mm});
            skLineSegment(sketch, "E94.MirrorCS", {"start": v(14.27, -117.07) * mm, "end": v(14.27, -108) * mm});
            skSolve(sketch);
        }
        {
            var Q0;
            Q0=makeQuery(id+"F16.imprint","IMPRINT",FACE,{"disambiguationData":[TD([[makeQuery(id+"F16.imprint","IMPRINT",EDGE,{"derivedFrom":sQuery(id+"F16.wireOp",EDGE,"E80")}),1.0]])]});
            var Q1;
            Q1=makeQuery(id+"F16.imprint","IMPRINT",FACE,{"disambiguationData":[TD([[makeQuery(id+"F16.imprint","IMPRINT",EDGE,{"derivedFrom":sQuery(id+"F16.wireOp",EDGE,"E93.MirrorC")}),1.0]])]});
            var Q2;
            Q2=makeQuery(id+"F2.opExtrude","CAP_FACE",FACE,{"disambiguationData":[OSD([sQuery(id+"F0.wireOp",EDGE,"E12"),sQuery(id+"F0.wireOp",EDGE,"E13"),sQuery(id+"F0.wireOp",EDGE,"E14"),sQuery(id+"F0.wireOp",EDGE,"E15"),sQuery(id+"F0.wireOp",EDGE,"E17.filletArc"),sQuery(id+"F0.wireOp",EDGE,"E18.filletArc"),sQuery(id+"F0.wireOp",EDGE,"E19.filletArc"),sQuery(id+"F0.wireOp",EDGE,"E20.filletArc"),sQuery(id+"F0.wireOp",EDGE,"E25.0"),sQuery(id+"F0.wireOp",EDGE,"E25.1"),sQuery(id+"F0.wireOp",EDGE,"E25.2"),sQuery(id+"F0.wireOp",EDGE,"E25.3"),sQuery(id+"F0.wireOp",EDGE,"E25.4"),sQuery(id+"F0.wireOp",EDGE,"E25.5"),sQuery(id+"F0.wireOp",EDGE,"E25.6"),sQuery(id+"F0.wireOp",EDGE,"E25.7")])],"isStart":false});
            extrude(context, id + "F17", {"entities" : qUnion([Q0, Q1]), "endBound" : BoundingType.UP_TO_SURFACE, "endBoundEntityFace" : qUnion([Q2]), "depth" : 25 * mm});
        }
    });
